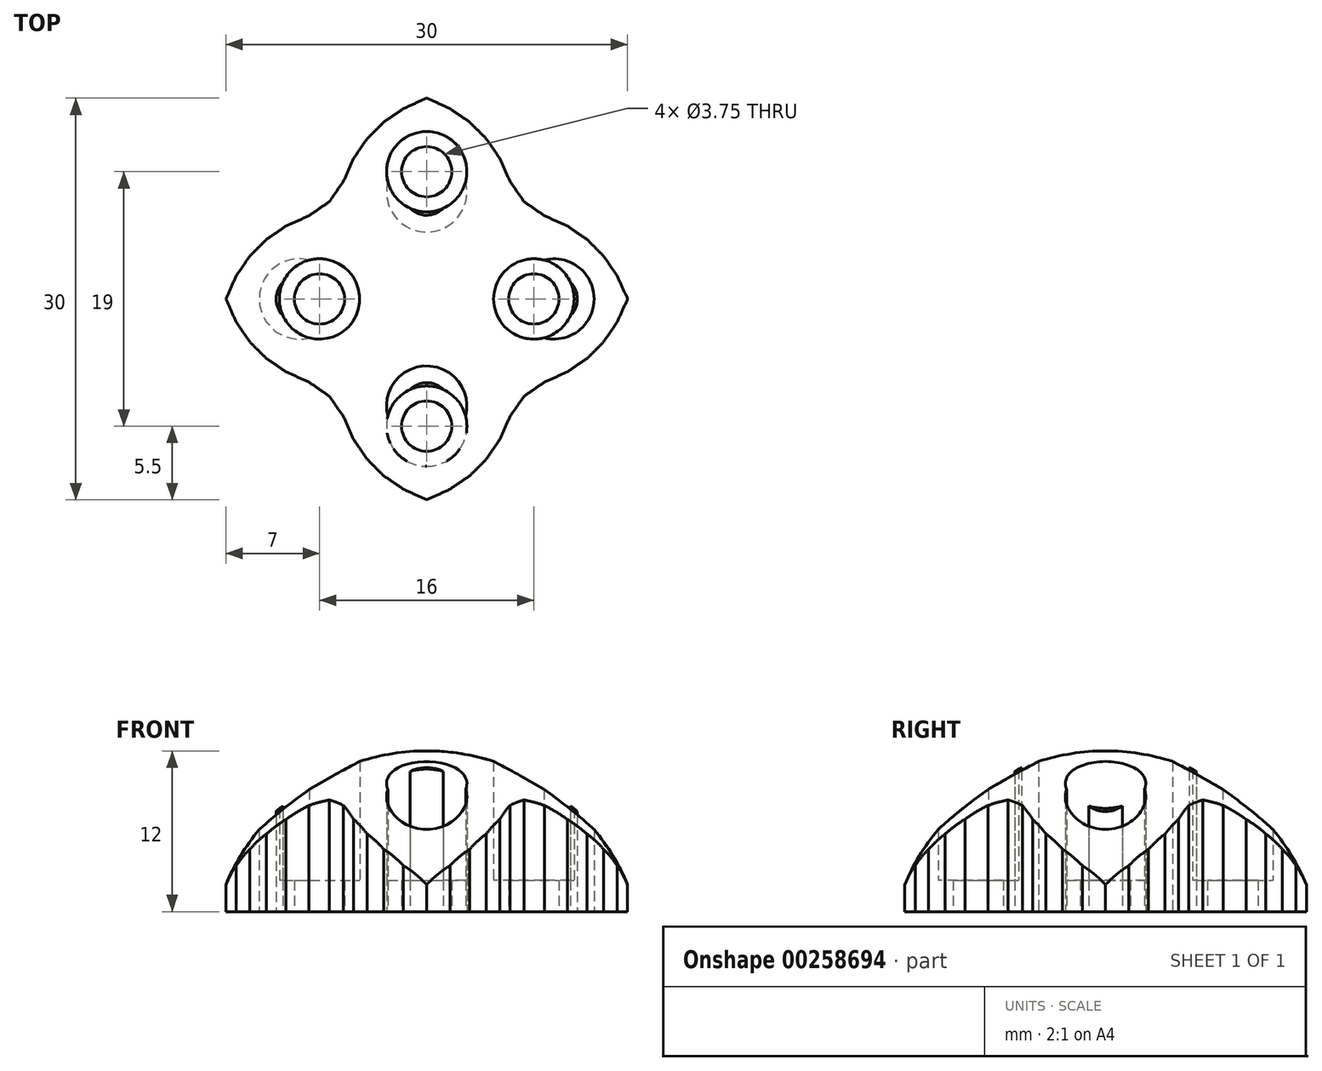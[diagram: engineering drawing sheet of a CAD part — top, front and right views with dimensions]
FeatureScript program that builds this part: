
annotation { "Feature Type Name" : "Feature", "Feature Type Description" : "" }
export const myFeature = defineFeature(function(context is Context, id is Id, definition is map)
    precondition{}
    {
        {
            var Q0;
            Q0=qCreatedBy(makeId("Front.planeOp"),FACE);
            var sketch = newSketch(context, id + "F0", { "sketchPlane" : qUnion([Q0])});
            skLineSegment(sketch, "E0", {"start": v(0, 0) * mm, "end": v(15, 0) * mm});
            skLineSegment(sketch, "E1", {"start": v(0, 0) * mm, "end": v(0, 10) * mm});
            skLineSegment(sketch, "E2", {"start": v(0, 0) * mm, "end": v(-15, 0) * mm});
            skArc(sketch, "E3", {"start": v(15, 0) * mm, "mid": v(0, 10) * mm, "end": v(-15, 0) * mm});
            skSolve(sketch);
        }
        {
            var Q0;
            {var subQ0=sQuery(id+"F0.wireOp",EDGE,"E0");Q0=makeQuery(id+"F0.imprint","IMPRINT",FACE,{"disambiguationData":[TD([[makeQuery(id+"F0.imprint","IMPRINT",EDGE,{"derivedFrom":subQ0}),1.0]])]});}
            var Q1;
            Q1=sQuery(id+"F0.wireOp",EDGE,"E1");
            var Q2;
            Q2=sQuery(id+"F0.wireOp",EDGE,"E1");
            revolve(context, id + "F1", {"entities" : qUnion([Q0]), "surfaceEntities" : qUnion([Q1]), "axis" : qUnion([Q2]), "revolveType" : RevolveType.FULL});
        }
        {
            var Q0;
            Q0=makeQuery(id+"F1.opRevolve","SWEPT_FACE",FACE,{"disambiguationData":[OSD([sQuery(id+"F0.wireOp",EDGE,"E0")])]});
            var sketch = newSketch(context, id + "F2", { "sketchPlane" : qUnion([Q0])});
            skLineSegment(sketch, "E4", {"start": v(-15, 0) * mm, "end": v(15, 0) * mm});
            skLineSegment(sketch, "E5", {"start": v(0, 15) * mm, "end": v(0, -15) * mm});
            skLineSegment(sketch, "E6", {"start": v(0, 0) * mm, "end": v(0, 8) * mm});
            skLineSegment(sketch, "E7", {"start": v(0, 0) * mm, "end": v(9.5, 0) * mm});
            skLineSegment(sketch, "E8", {"start": v(0, 0) * mm, "end": v(0, -8) * mm});
            skLineSegment(sketch, "E9", {"start": v(0, 0) * mm, "end": v(-9.5, 0) * mm});
            skCircle(sketch, "E10", {"center": v(-9.5, 0) * mm, "radius": 1.75 * mm});
            skCircle(sketch, "E11", {"center": v(0, 8) * mm, "radius": 1.75 * mm});
            skCircle(sketch, "E12", {"center": v(9.5, 0) * mm, "radius": 1.75 * mm});
            skCircle(sketch, "E13", {"center": v(0, -8) * mm, "radius": 1.75 * mm});
            skCircle(sketch, "E14", {"center": v(9.5, 0) * mm, "radius": 3 * mm});
            skCircle(sketch, "E15", {"center": v(0, 8) * mm, "radius": 3 * mm});
            skCircle(sketch, "E16", {"center": v(-9.5, 0) * mm, "radius": 3 * mm});
            skCircle(sketch, "E17", {"center": v(0, -8) * mm, "radius": 3 * mm});
            skLineSegment(sketch, "E18", {"start": v(0, 15) * mm, "end": v(15, 0) * mm});
            skLineSegment(sketch, "E19", {"start": v(15, 0) * mm, "end": v(0, -15) * mm});
            skLineSegment(sketch, "E20", {"start": v(0, -15) * mm, "end": v(-15, 0) * mm});
            skLineSegment(sketch, "E21", {"start": v(-1.74, 14.21) * mm, "end": v(0, 15) * mm});
            skLineSegment(sketch, "E22", {"start": v(-1.74, 14.21) * mm, "end": v(-3.2, 13.2) * mm});
            skLineSegment(sketch, "E23", {"start": v(-15, 0) * mm, "end": v(-14.21, 1.74) * mm});
            skLineSegment(sketch, "E24", {"start": v(-14.21, 1.74) * mm, "end": v(-13.2, 3.2) * mm});
            skLineSegment(sketch, "E25", {"start": v(-7.27, 7.27) * mm, "end": v(-6.21, 8.79) * mm});
            skLineSegment(sketch, "E26", {"start": v(-3.2, 13.2) * mm, "end": v(-4.45, 11.97) * mm});
            skLineSegment(sketch, "E27", {"start": v(-4.45, 11.97) * mm, "end": v(-5.45, 10.5) * mm});
            skLineSegment(sketch, "E28", {"start": v(-5.45, 10.5) * mm, "end": v(-6.21, 8.79) * mm});
            skLineSegment(sketch, "E29", {"start": v(-7.27, 7.27) * mm, "end": v(-8.79, 6.21) * mm});
            skLineSegment(sketch, "E30", {"start": v(-8.79, 6.21) * mm, "end": v(-10.5, 5.45) * mm});
            skLineSegment(sketch, "E31", {"start": v(-10.5, 5.45) * mm, "end": v(-11.97, 4.45) * mm});
            skLineSegment(sketch, "E32", {"start": v(-11.97, 4.45) * mm, "end": v(-13.2, 3.2) * mm});
            skSolve(sketch);
        }
        {
            var Q0;
            {var subQ1=sQuery(id+"F2.wireOp",EDGE,"E21");Q0=makeQuery(id+"F2.imprint","IMPRINT",FACE,{"disambiguationData":[TD([[makeQuery(id+"F2.imprint","IMPRINT",EDGE,{"derivedFrom":subQ1}),1.0]])]});}
            var Q1;
            {var subQ0=sQuery(id+"F2.wireOp",EDGE,"E18");Q1=makeQuery(id+"F2.imprint","IMPRINT",FACE,{"disambiguationData":[TD([[makeQuery(id+"F2.imprint","IMPRINT",EDGE,{"derivedFrom":subQ0}),1.0]])]});}
            var Q2;
            {var subQ0=sQuery(id+"F2.wireOp",EDGE,"E15");var subQ1=sQuery(id+"F2.wireOp",EDGE,"E5");var subQ2=makeQuery(id+"F2.imprint","INTERSECT",VERTEX,{"derivedFrom":[subQ1,subQ0]});Q2=makeQuery(id+"F2.imprint","IMPRINT",FACE,{"disambiguationData":[TD([[makeQuery(id+"F2.imprint","IMPRINT",EDGE,{"disambiguationData":[TD([[subQ2,-1.0]])],"derivedFrom":subQ1}),1.0]])]});}
            var Q3;
            {var subQ0=sQuery(id+"F2.wireOp",EDGE,"E6");var subQ1=sQuery(id+"F2.wireOp",EDGE,"E5");var subQ2=makeQuery(id+"F2.imprint","INTERSECT",VERTEX,{"derivedFrom":[subQ1,subQ0]});Q3=makeQuery(id+"F2.imprint","IMPRINT",FACE,{"disambiguationData":[TD([[makeQuery(id+"F2.imprint","IMPRINT",EDGE,{"disambiguationData":[TD([[subQ2,1.0]])],"derivedFrom":subQ1}),1.0]])]});}
            var Q4;
            {var subQ7=sQuery(id+"F2.wireOp",EDGE,"E18");Q4=makeQuery(id+"F2.imprint","IMPRINT",FACE,{"disambiguationData":[TD([[makeQuery(id+"F2.imprint","IMPRINT",EDGE,{"derivedFrom":subQ7}),-1.0]])]});}
            var Q5;
            {var subQ7=sQuery(id+"F2.wireOp",EDGE,"E20");Q5=makeQuery(id+"F2.imprint","IMPRINT",FACE,{"disambiguationData":[TD([[makeQuery(id+"F2.imprint","IMPRINT",EDGE,{"derivedFrom":subQ7}),-1.0]])]});}
            var Q6;
            {var subQ0=sQuery(id+"F2.wireOp",EDGE,"E16");var subQ1=sQuery(id+"F2.wireOp",EDGE,"E4");var subQ2=makeQuery(id+"F2.imprint","INTERSECT",VERTEX,{"derivedFrom":[subQ1,subQ0]});Q6=makeQuery(id+"F2.imprint","IMPRINT",FACE,{"disambiguationData":[TD([[makeQuery(id+"F2.imprint","IMPRINT",EDGE,{"disambiguationData":[TD([[subQ2,-1.0]])],"derivedFrom":subQ1}),-1.0]])]});}
            var Q7;
            {var subQ0=sQuery(id+"F2.wireOp",EDGE,"E9");var subQ1=sQuery(id+"F2.wireOp",EDGE,"E4");var subQ2=makeQuery(id+"F2.imprint","INTERSECT",VERTEX,{"derivedFrom":[subQ1,subQ0]});Q7=makeQuery(id+"F2.imprint","IMPRINT",FACE,{"disambiguationData":[TD([[makeQuery(id+"F2.imprint","IMPRINT",EDGE,{"disambiguationData":[TD([[subQ2,1.0]])],"derivedFrom":subQ1}),-1.0]])]});}
            var Q8;
            {var subQ0=sQuery(id+"F2.wireOp",EDGE,"E20");Q8=makeQuery(id+"F2.imprint","IMPRINT",FACE,{"disambiguationData":[TD([[makeQuery(id+"F2.imprint","IMPRINT",EDGE,{"derivedFrom":subQ0}),1.0]])]});}
            var Q9;
            {var subQ0=sQuery(id+"F2.wireOp",EDGE,"E8");var subQ1=sQuery(id+"F2.wireOp",EDGE,"E5");var subQ2=makeQuery(id+"F2.imprint","INTERSECT",VERTEX,{"derivedFrom":[subQ1,subQ0]});Q9=makeQuery(id+"F2.imprint","IMPRINT",FACE,{"disambiguationData":[TD([[makeQuery(id+"F2.imprint","IMPRINT",EDGE,{"disambiguationData":[TD([[subQ2,-1.0]])],"derivedFrom":subQ1}),-1.0]])]});}
            var Q10;
            {var subQ0=sQuery(id+"F2.wireOp",EDGE,"E13");var subQ1=sQuery(id+"F2.wireOp",EDGE,"E5");var subQ2=makeQuery(id+"F2.imprint","INTERSECT",VERTEX,{"derivedFrom":[subQ1,subQ0]});Q10=makeQuery(id+"F2.imprint","IMPRINT",FACE,{"disambiguationData":[TD([[makeQuery(id+"F2.imprint","IMPRINT",EDGE,{"disambiguationData":[TD([[subQ2,-1.0]])],"derivedFrom":subQ1}),-1.0]])]});}
            var Q11;
            {var subQ0=sQuery(id+"F2.wireOp",EDGE,"E8");var subQ1=sQuery(id+"F2.wireOp",EDGE,"E5");var subQ2=makeQuery(id+"F2.imprint","INTERSECT",VERTEX,{"derivedFrom":[subQ1,subQ0]});Q11=makeQuery(id+"F2.imprint","IMPRINT",FACE,{"disambiguationData":[TD([[makeQuery(id+"F2.imprint","IMPRINT",EDGE,{"disambiguationData":[TD([[subQ2,-1.0]])],"derivedFrom":subQ1}),1.0]])]});}
            var Q12;
            {var subQ0=sQuery(id+"F2.wireOp",EDGE,"E13");var subQ1=sQuery(id+"F2.wireOp",EDGE,"E5");var subQ2=makeQuery(id+"F2.imprint","INTERSECT",VERTEX,{"derivedFrom":[subQ1,subQ0]});Q12=makeQuery(id+"F2.imprint","IMPRINT",FACE,{"disambiguationData":[TD([[makeQuery(id+"F2.imprint","IMPRINT",EDGE,{"disambiguationData":[TD([[subQ2,-1.0]])],"derivedFrom":subQ1}),1.0]])]});}
            var Q13;
            {var subQ5=sQuery(id+"F2.wireOp",EDGE,"E19");Q13=makeQuery(id+"F2.imprint","IMPRINT",FACE,{"disambiguationData":[TD([[makeQuery(id+"F2.imprint","IMPRINT",EDGE,{"derivedFrom":subQ5}),-1.0]])]});}
            var Q14;
            {var subQ0=sQuery(id+"F2.wireOp",EDGE,"E7");var subQ1=sQuery(id+"F2.wireOp",EDGE,"E4");var subQ2=makeQuery(id+"F2.imprint","INTERSECT",VERTEX,{"derivedFrom":[subQ1,subQ0]});Q14=makeQuery(id+"F2.imprint","IMPRINT",FACE,{"disambiguationData":[TD([[makeQuery(id+"F2.imprint","IMPRINT",EDGE,{"disambiguationData":[TD([[subQ2,-1.0]])],"derivedFrom":subQ1}),-1.0]])]});}
            var Q15;
            {var subQ0=sQuery(id+"F2.wireOp",EDGE,"E12");var subQ1=sQuery(id+"F2.wireOp",EDGE,"E4");var subQ2=makeQuery(id+"F2.imprint","INTERSECT",VERTEX,{"derivedFrom":[subQ1,subQ0]});Q15=makeQuery(id+"F2.imprint","IMPRINT",FACE,{"disambiguationData":[TD([[makeQuery(id+"F2.imprint","IMPRINT",EDGE,{"disambiguationData":[TD([[subQ2,-1.0]])],"derivedFrom":subQ1}),1.0]])]});}
            var Q16;
            {var subQ0=sQuery(id+"F2.wireOp",EDGE,"E12");var subQ1=sQuery(id+"F2.wireOp",EDGE,"E4");var subQ2=makeQuery(id+"F2.imprint","INTERSECT",VERTEX,{"derivedFrom":[subQ1,subQ0]});Q16=makeQuery(id+"F2.imprint","IMPRINT",FACE,{"disambiguationData":[TD([[makeQuery(id+"F2.imprint","IMPRINT",EDGE,{"disambiguationData":[TD([[subQ2,-1.0]])],"derivedFrom":subQ1}),-1.0]])]});}
            var Q17;
            {var subQ0=sQuery(id+"F2.wireOp",EDGE,"E7");var subQ1=sQuery(id+"F2.wireOp",EDGE,"E4");var subQ2=makeQuery(id+"F2.imprint","INTERSECT",VERTEX,{"derivedFrom":[subQ1,subQ0]});Q17=makeQuery(id+"F2.imprint","IMPRINT",FACE,{"disambiguationData":[TD([[makeQuery(id+"F2.imprint","IMPRINT",EDGE,{"disambiguationData":[TD([[subQ2,-1.0]])],"derivedFrom":subQ1}),1.0]])]});}
            var Q18;
            {var subQ0=sQuery(id+"F2.wireOp",EDGE,"E19");Q18=makeQuery(id+"F2.imprint","IMPRINT",FACE,{"disambiguationData":[TD([[makeQuery(id+"F2.imprint","IMPRINT",EDGE,{"derivedFrom":subQ0}),1.0]])]});}
            extrude(context, id + "F3", {"entities" : qUnion([Q0, Q1, Q2, Q3, Q4, Q5, Q6, Q7, Q8, Q9, Q10, Q11, Q12, Q13, Q14, Q15, Q16, Q17, Q18]), "operationType" : NewBodyOperationType.REMOVE, "oppositeDirection" : true, "depth" : 25 * mm});
        }
        {
            var Q0;
            Q0=makeQuery(id+"F1.opRevolve","SWEPT_BODY",BODY,{"disambiguationData":[OSD([sQuery(id+"F0.wireOp",EDGE,"E0"),sQuery(id+"F0.wireOp",EDGE,"E1"),sQuery(id+"F0.wireOp",EDGE,"E3")])]});
            var Q1;
            Q1=makeQuery(id+"F3.boolean.opBoolean","COPY",FACE,{"derivedFrom":makeQuery(id+"F3.opExtrude","SWEPT_FACE",FACE,{"disambiguationData":[OSD([sQuery(id+"F2.wireOp",EDGE,"E4"),sQuery(id+"F2.wireOp",EDGE,"E9")])]})});
            mirror(context, id + "F4", {"operationType" : NewBodyOperationType.ADD, "entities" : qUnion([Q0]), "mirrorPlane" : qUnion([Q1])});
        }
        {
            var Q0;
            Q0=makeQuery(id+"F1.opRevolve","SWEPT_BODY",BODY,{"disambiguationData":[OSD([sQuery(id+"F0.wireOp",EDGE,"E0"),sQuery(id+"F0.wireOp",EDGE,"E1"),sQuery(id+"F0.wireOp",EDGE,"E3")])]});
            var Q1;
            {var subQ0=makeQuery(id+"F3.boolean.opBoolean","COPY",FACE,{"derivedFrom":makeQuery(id+"F3.opExtrude","SWEPT_FACE",FACE,{"disambiguationData":[OSD([sQuery(id+"F2.wireOp",EDGE,"E5"),sQuery(id+"F2.wireOp",EDGE,"E6")])]})});Q1=makeQuery(id+"F4.boolean.opBoolean","MERGE",FACE,{"derivedFrom":[subQ0,makeQuery(id+"F4.opPattern","COPY",FACE,{"derivedFrom":subQ0,"instanceName":"1"})]});}
            mirror(context, id + "F5", {"operationType" : NewBodyOperationType.ADD, "entities" : qUnion([Q0]), "mirrorPlane" : qUnion([Q1])});
        }
        {
            var Q0;
            {var subQ0=makeQuery(id+"F1.opRevolve","SWEPT_FACE",FACE,{"disambiguationData":[OSD([sQuery(id+"F0.wireOp",EDGE,"E0")])]});var subQ1=makeQuery(id+"F4.boolean.opBoolean","MERGE",FACE,{"derivedFrom":[subQ0,makeQuery(id+"F4.opPattern","COPY",FACE,{"derivedFrom":subQ0,"instanceName":"1"})]});Q0=makeQuery(id+"F5.boolean.opBoolean","MERGE",FACE,{"derivedFrom":[subQ1,makeQuery(id+"F5.opPattern","COPY",FACE,{"derivedFrom":subQ1,"instanceName":"1"})]});}
            var sketch = newSketch(context, id + "F6", { "sketchPlane" : qUnion([Q0])});
            skCircle(sketch, "E33", {"center": v(0, 9.5) * mm, "radius": 3 * mm});
            skCircle(sketch, "E34", {"center": v(0, 9.5) * mm, "radius": 1.75 * mm});
            skCircle(sketch, "E35", {"center": v(8, 0) * mm, "radius": 1.75 * mm});
            skCircle(sketch, "E36", {"center": v(8, 0) * mm, "radius": 3 * mm});
            skCircle(sketch, "E37", {"center": v(0, -9.5) * mm, "radius": 3 * mm});
            skCircle(sketch, "E38", {"center": v(0, -9.5) * mm, "radius": 1.75 * mm});
            skCircle(sketch, "E39", {"center": v(-8, 0) * mm, "radius": 1.75 * mm});
            skCircle(sketch, "E40", {"center": v(-8, 0) * mm, "radius": 3 * mm});
            skSolve(sketch);
        }
        {
            var Q0;
            Q0=makeQuery(id+"F6.imprint","IMPRINT",FACE,{"disambiguationData":[TD([[makeQuery(id+"F6.imprint","IMPRINT",EDGE,{"derivedFrom":sQuery(id+"F6.wireOp",EDGE,"E34")}),1.0]])]});
            var Q1;
            Q1=makeQuery(id+"F6.imprint","IMPRINT",FACE,{"disambiguationData":[TD([[makeQuery(id+"F6.imprint","IMPRINT",EDGE,{"derivedFrom":sQuery(id+"F6.wireOp",EDGE,"E35")}),1.0]])]});
            var Q2;
            Q2=makeQuery(id+"F6.imprint","IMPRINT",FACE,{"disambiguationData":[TD([[makeQuery(id+"F6.imprint","IMPRINT",EDGE,{"derivedFrom":sQuery(id+"F6.wireOp",EDGE,"E39")}),1.0]])]});
            var Q3;
            Q3=makeQuery(id+"F6.imprint","IMPRINT",FACE,{"disambiguationData":[TD([[makeQuery(id+"F6.imprint","IMPRINT",EDGE,{"derivedFrom":sQuery(id+"F6.wireOp",EDGE,"E38")}),1.0]])]});
            extrude(context, id + "F7", {"entities" : qUnion([Q0, Q1, Q2, Q3]), "operationType" : NewBodyOperationType.REMOVE, "oppositeDirection" : true, "depth" : 25 * mm});
        }
        {
            var Q0;
            Q0=makeQuery(id+"F6.imprint","IMPRINT",FACE,{"disambiguationData":[TD([[makeQuery(id+"F6.imprint","IMPRINT",EDGE,{"derivedFrom":sQuery(id+"F6.wireOp",EDGE,"E33")}),1.0]])]});
            var Q1;
            Q1=makeQuery(id+"F6.imprint","IMPRINT",FACE,{"disambiguationData":[TD([[makeQuery(id+"F6.imprint","IMPRINT",EDGE,{"derivedFrom":sQuery(id+"F6.wireOp",EDGE,"E35")}),-1.0]])]});
            var Q2;
            Q2=makeQuery(id+"F6.imprint","IMPRINT",FACE,{"disambiguationData":[TD([[makeQuery(id+"F6.imprint","IMPRINT",EDGE,{"derivedFrom":sQuery(id+"F6.wireOp",EDGE,"E37")}),1.0]])]});
            var Q3;
            Q3=makeQuery(id+"F6.imprint","IMPRINT",FACE,{"disambiguationData":[TD([[makeQuery(id+"F6.imprint","IMPRINT",EDGE,{"derivedFrom":sQuery(id+"F6.wireOp",EDGE,"E39")}),-1.0]])]});
            extrude(context, id + "F8", {"entities" : qUnion([Q0, Q1, Q2, Q3]), "operationType" : NewBodyOperationType.REMOVE, "oppositeDirection" : true, "depth" : 25 * mm});
        }
        {
            var Q0;
            Q0=makeQuery(id+"F6.imprint","IMPRINT",FACE,{"disambiguationData":[TD([[makeQuery(id+"F6.imprint","IMPRINT",EDGE,{"derivedFrom":sQuery(id+"F6.wireOp",EDGE,"E33")}),1.0]])]});
            var Q1;
            Q1=makeQuery(id+"F6.imprint","IMPRINT",FACE,{"disambiguationData":[TD([[makeQuery(id+"F6.imprint","IMPRINT",EDGE,{"derivedFrom":sQuery(id+"F6.wireOp",EDGE,"E35")}),-1.0]])]});
            var Q2;
            Q2=makeQuery(id+"F6.imprint","IMPRINT",FACE,{"disambiguationData":[TD([[makeQuery(id+"F6.imprint","IMPRINT",EDGE,{"derivedFrom":sQuery(id+"F6.wireOp",EDGE,"E39")}),-1.0]])]});
            var Q3;
            Q3=makeQuery(id+"F6.imprint","IMPRINT",FACE,{"disambiguationData":[TD([[makeQuery(id+"F6.imprint","IMPRINT",EDGE,{"derivedFrom":sQuery(id+"F6.wireOp",EDGE,"E37")}),1.0]])]});
            extrude(context, id + "F9", {"entities" : qUnion([Q0, Q1, Q2, Q3]), "operationType" : NewBodyOperationType.ADD, "oppositeDirection" : true, "depth" : .33 * mm});
        }
        {
            var Q0;
            {var subQ0=makeQuery(id+"F1.opRevolve","SWEPT_FACE",FACE,{"disambiguationData":[OSD([sQuery(id+"F0.wireOp",EDGE,"E0")])]});var subQ1=makeQuery(id+"F4.boolean.opBoolean","MERGE",FACE,{"derivedFrom":[subQ0,makeQuery(id+"F4.opPattern","COPY",FACE,{"derivedFrom":subQ0,"instanceName":"1"})]});Q0=makeQuery(id+"F9.boolean.opBoolean","MERGE",FACE,{"derivedFrom":[makeQuery(id+"F5.boolean.opBoolean","MERGE",FACE,{"derivedFrom":[subQ1,makeQuery(id+"F5.opPattern","COPY",FACE,{"derivedFrom":subQ1,"instanceName":"1"})]}),makeQuery(id+"F9.opExtrude","CAP_FACE",FACE,{"disambiguationData":[OSD([sQuery(id+"F6.wireOp",EDGE,"E33"),sQuery(id+"F6.wireOp",EDGE,"E34")])],"isStart":true}),makeQuery(id+"F9.opExtrude","CAP_FACE",FACE,{"disambiguationData":[OSD([sQuery(id+"F6.wireOp",EDGE,"E35"),sQuery(id+"F6.wireOp",EDGE,"E36")])],"isStart":true}),makeQuery(id+"F9.opExtrude","CAP_FACE",FACE,{"disambiguationData":[OSD([sQuery(id+"F6.wireOp",EDGE,"E37"),sQuery(id+"F6.wireOp",EDGE,"E38")])],"isStart":true}),makeQuery(id+"F9.opExtrude","CAP_FACE",FACE,{"disambiguationData":[OSD([sQuery(id+"F6.wireOp",EDGE,"E39"),sQuery(id+"F6.wireOp",EDGE,"E40")])],"isStart":true})]});}
            extrude(context, id + "F10", {"entities" : qUnion([Q0]), "operationType" : NewBodyOperationType.ADD, "depth" : 2 * mm});
        }
        {
            var Q0;
            Q0=makeQuery(id+"F10.opExtrude","CAP_FACE",FACE,{"disambiguationData":[OSD([sQuery(id+"F0.wireOp",EDGE,"E0"),sQuery(id+"F6.wireOp",EDGE,"E33"),sQuery(id+"F6.wireOp",EDGE,"E34"),sQuery(id+"F6.wireOp",EDGE,"E35"),sQuery(id+"F6.wireOp",EDGE,"E36"),sQuery(id+"F6.wireOp",EDGE,"E37"),sQuery(id+"F6.wireOp",EDGE,"E38"),sQuery(id+"F6.wireOp",EDGE,"E39"),sQuery(id+"F6.wireOp",EDGE,"E40")])],"isStart":false});
            var sketch = newSketch(context, id + "F11", { "sketchPlane" : qUnion([Q0])});
            skCircle(sketch, "E41", {"center": v(-8, 0) * mm, "radius": 1.88 * mm});
            skCircle(sketch, "E42", {"center": v(8, 0) * mm, "radius": 1.88 * mm});
            skCircle(sketch, "E43", {"center": v(0, -9.5) * mm, "radius": 1.88 * mm});
            skCircle(sketch, "E44", {"center": v(0, 9.5) * mm, "radius": 1.88 * mm});
            skSolve(sketch);
        }
        {
            var Q0;
            Q0=makeQuery(id+"F11.imprint","IMPRINT",FACE,{"disambiguationData":[TD([[makeQuery(id+"F11.imprint","IMPRINT",EDGE,{"derivedFrom":sQuery(id+"F11.wireOp",EDGE,"E44")}),1.0]])]});
            var Q1;
            Q1=makeQuery(id+"F11.imprint","IMPRINT",FACE,{"disambiguationData":[TD([[makeQuery(id+"F11.imprint","IMPRINT",EDGE,{"derivedFrom":sQuery(id+"F11.wireOp",EDGE,"E42")}),1.0]])]});
            var Q2;
            Q2=makeQuery(id+"F11.imprint","IMPRINT",FACE,{"disambiguationData":[TD([[makeQuery(id+"F11.imprint","IMPRINT",EDGE,{"derivedFrom":sQuery(id+"F11.wireOp",EDGE,"E41")}),1.0]])]});
            var Q3;
            Q3=makeQuery(id+"F11.imprint","IMPRINT",FACE,{"disambiguationData":[TD([[makeQuery(id+"F11.imprint","IMPRINT",EDGE,{"derivedFrom":sQuery(id+"F11.wireOp",EDGE,"E43")}),1.0]])]});
            extrude(context, id + "F12", {"entities" : qUnion([Q0, Q1, Q2, Q3]), "operationType" : NewBodyOperationType.REMOVE, "oppositeDirection" : true, "depth" : 25 * mm});
        }
    });
